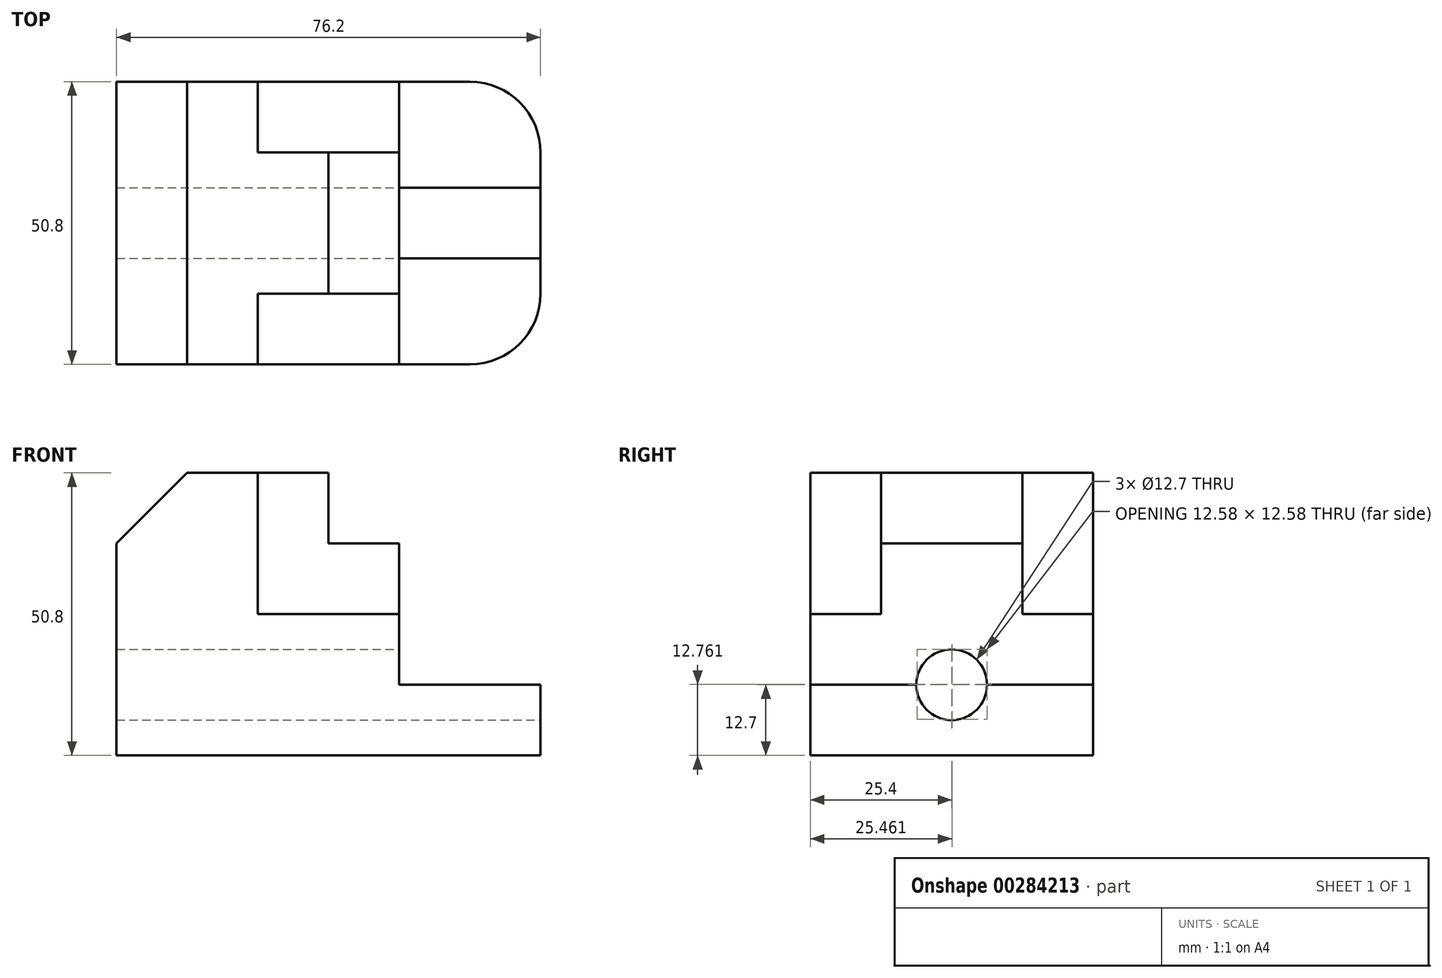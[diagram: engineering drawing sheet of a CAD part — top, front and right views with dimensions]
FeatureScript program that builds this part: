
annotation { "Feature Type Name" : "Feature", "Feature Type Description" : "" }
export const myFeature = defineFeature(function(context is Context, id is Id, definition is map)
    precondition{}
    {
        {
            var Q0;
            Q0=qCreatedBy(makeId("Front.planeOp"),FACE);
            var sketch = newSketch(context, id + "F0", { "sketchPlane" : qUnion([Q0])});
            skLineSegment(sketch, "E0", {"start": v(0, 0) * mm, "end": v(0, 38.1) * mm});
            skLineSegment(sketch, "E1", {"start": v(0, 38.1) * mm, "end": v(12.7, 50.8) * mm});
            skLineSegment(sketch, "E2", {"start": v(12.7, 50.8) * mm, "end": v(38.1, 50.8) * mm});
            skLineSegment(sketch, "E3", {"start": v(38.1, 50.8) * mm, "end": v(38.1, 38.1) * mm});
            skLineSegment(sketch, "E4", {"start": v(38.1, 38.1) * mm, "end": v(50.8, 38.1) * mm});
            skLineSegment(sketch, "E5", {"start": v(50.8, 38.1) * mm, "end": v(50.8, 12.7) * mm});
            skLineSegment(sketch, "E6", {"start": v(50.8, 12.7) * mm, "end": v(76.2, 12.7) * mm});
            skLineSegment(sketch, "E7", {"start": v(76.2, 12.7) * mm, "end": v(76.2, 0) * mm});
            skLineSegment(sketch, "E8", {"start": v(76.2, 0) * mm, "end": v(0, 0) * mm});
            skSolve(sketch);
        }
        {
            var Q0;
            Q0=makeQuery(id+"F0.imprint","IMPRINT",FACE,{"disambiguationData":[TD([[makeQuery(id+"F0.imprint","IMPRINT",EDGE,{"derivedFrom":sQuery(id+"F0.wireOp",EDGE,"E0")}),-1.0]])]});
            extrude(context, id + "F1", {"entities" : qUnion([Q0]), "endBound" : BoundingType.SYMMETRIC, "depth" : 50.8 * mm});
        }
        {
            var Q0;
            Q0=makeQuery(id+"F1.opExtrude","SWEPT_FACE",FACE,{"disambiguationData":[OSD([sQuery(id+"F0.wireOp",EDGE,"E2")])]});
            var sketch = newSketch(context, id + "F2", { "sketchPlane" : qUnion([Q0])});
            skLineSegment(sketch, "E9.bottom", {"start": v(25.4, 25.4) * mm, "end": v(50.8, 25.4) * mm});
            skLineSegment(sketch, "E9.top", {"start": v(25.4, 12.7) * mm, "end": v(50.8, 12.7) * mm});
            skLineSegment(sketch, "E9.left", {"start": v(25.4, 25.4) * mm, "end": v(25.4, 12.7) * mm});
            skLineSegment(sketch, "E9.right", {"start": v(50.8, 25.4) * mm, "end": v(50.8, 12.7) * mm});
            skLineSegment(sketch, "E10.bottom", {"start": v(25.4, -25.4) * mm, "end": v(50.8, -25.4) * mm});
            skLineSegment(sketch, "E10.top", {"start": v(25.4, -12.7) * mm, "end": v(50.8, -12.7) * mm});
            skLineSegment(sketch, "E10.left", {"start": v(25.4, -25.4) * mm, "end": v(25.4, -12.7) * mm});
            skLineSegment(sketch, "E10.right", {"start": v(50.8, -25.4) * mm, "end": v(50.8, -12.7) * mm});
            skSolve(sketch);
        }
        {
            var Q0;
            {var subQ4=sQuery(id+"F2.wireOp",EDGE,"E9.left");Q0=makeQuery(id+"F2.imprint","IMPRINT",FACE,{"disambiguationData":[TD([[makeQuery(id+"F2.imprint","IMPRINT",EDGE,{"derivedFrom":subQ4}),1.0]])]});}
            extrude(context, id + "F3", {"entities" : qUnion([Q0]), "operationType" : NewBodyOperationType.REMOVE, "oppositeDirection" : true, "depth" : 25.4 * mm});
        }
        {
            var Q0;
            {var subQ4=sQuery(id+"F2.wireOp",EDGE,"E10.left");Q0=makeQuery(id+"F2.imprint","IMPRINT",FACE,{"disambiguationData":[TD([[makeQuery(id+"F2.imprint","IMPRINT",EDGE,{"derivedFrom":subQ4}),-1.0]])]});}
            extrude(context, id + "F4", {"entities" : qUnion([Q0]), "operationType" : NewBodyOperationType.REMOVE, "oppositeDirection" : true, "depth" : 25.4 * mm});
        }
        {
            var Q0;
            Q0=makeQuery(id+"F1.opExtrude","CAP_FACE",FACE,{"disambiguationData":[OSD([sQuery(id+"F0.wireOp",EDGE,"E0"),sQuery(id+"F0.wireOp",EDGE,"E1"),sQuery(id+"F0.wireOp",EDGE,"E2"),sQuery(id+"F0.wireOp",EDGE,"E3"),sQuery(id+"F0.wireOp",EDGE,"E4"),sQuery(id+"F0.wireOp",EDGE,"E5"),sQuery(id+"F0.wireOp",EDGE,"E6"),sQuery(id+"F0.wireOp",EDGE,"E7"),sQuery(id+"F0.wireOp",EDGE,"E8")])],"isStart":false});
            var sketch = newSketch(context, id + "F5", { "sketchPlane" : qUnion([Q0])});
            skLineSegment(sketch, "E11.bottom", {"start": v(38.1, 38.1) * mm, "end": v(50.8, 38.1) * mm});
            skLineSegment(sketch, "E11.top", {"start": v(38.1, 25.4) * mm, "end": v(50.8, 25.4) * mm});
            skLineSegment(sketch, "E11.left", {"start": v(38.1, 38.1) * mm, "end": v(38.1, 25.4) * mm});
            skLineSegment(sketch, "E11.right", {"start": v(50.8, 38.1) * mm, "end": v(50.8, 25.4) * mm});
            skSolve(sketch);
        }
        {
            var Q0;
            Q0=makeQuery(id+"F5.imprint","IMPRINT",FACE,{"disambiguationData":[TD([[makeQuery(id+"F5.imprint","IMPRINT",EDGE,{"derivedFrom":sQuery(id+"F5.wireOp",EDGE,"E11.bottom")}),-1.0]])]});
            extrude(context, id + "F6", {"entities" : qUnion([Q0]), "operationType" : NewBodyOperationType.REMOVE, "oppositeDirection" : true, "depth" : 12.7 * mm});
        }
        {
            var Q0;
            Q0=makeQuery(id+"F1.opExtrude","CAP_FACE",FACE,{"disambiguationData":[OSD([sQuery(id+"F0.wireOp",EDGE,"E0"),sQuery(id+"F0.wireOp",EDGE,"E1"),sQuery(id+"F0.wireOp",EDGE,"E2"),sQuery(id+"F0.wireOp",EDGE,"E3"),sQuery(id+"F0.wireOp",EDGE,"E4"),sQuery(id+"F0.wireOp",EDGE,"E5"),sQuery(id+"F0.wireOp",EDGE,"E6"),sQuery(id+"F0.wireOp",EDGE,"E7"),sQuery(id+"F0.wireOp",EDGE,"E8")])],"isStart":true});
            var sketch = newSketch(context, id + "F7", { "sketchPlane" : qUnion([Q0])});
            skLineSegment(sketch, "E12.bottom", {"start": v(-50.8, 38.1) * mm, "end": v(-38.1, 38.1) * mm});
            skLineSegment(sketch, "E12.top", {"start": v(-50.8, 25.4) * mm, "end": v(-38.1, 25.4) * mm});
            skLineSegment(sketch, "E12.left", {"start": v(-50.8, 38.1) * mm, "end": v(-50.8, 25.4) * mm});
            skLineSegment(sketch, "E12.right", {"start": v(-38.1, 38.1) * mm, "end": v(-38.1, 25.4) * mm});
            skSolve(sketch);
        }
        {
            var Q0;
            Q0=makeQuery(id+"F7.imprint","IMPRINT",FACE,{"disambiguationData":[TD([[makeQuery(id+"F7.imprint","IMPRINT",EDGE,{"derivedFrom":sQuery(id+"F7.wireOp",EDGE,"E12.bottom")}),1.0]])]});
            extrude(context, id + "F8", {"entities" : qUnion([Q0]), "operationType" : NewBodyOperationType.REMOVE, "oppositeDirection" : true, "depth" : 12.7 * mm});
        }
        {
            var Q0;
            Q0=makeQuery(id+"F1.opExtrude","SWEPT_FACE",FACE,{"disambiguationData":[OSD([sQuery(id+"F0.wireOp",EDGE,"E7")])]});
            var sketch = newSketch(context, id + "F9", { "sketchPlane" : qUnion([Q0])});
            skCircle(sketch, "E13", {"center": v(0, 12.7) * mm, "radius": 6.35 * mm});
            skSolve(sketch);
        }
        {
            var Q0;
            {var subQ0=sQuery(id+"F9.wireOp",EDGE,"E13");var subQ1=makeQuery(id+"F1.opExtrude","SWEPT_EDGE",EDGE,{"disambiguationData":[OSD([sQuery(id+"F0.wireOp",EDGE,"E6"),sQuery(id+"F0.wireOp",EDGE,"E7")])]});var subQ2=makeQuery(id+"F9.imprint","INTERSECT",VERTEX,{"disambiguationData":[OD(0.0)],"derivedFrom":[subQ1,subQ0]});Q0=makeQuery(id+"F9.imprint","IMPRINT",FACE,{"disambiguationData":[TD([[makeQuery(id+"F9.imprint","IMPRINT",EDGE,{"disambiguationData":[TD([[subQ2,1.0]])],"derivedFrom":subQ0}),1.0]])]});}
            var Q1;
            {var subQ0=sQuery(id+"F9.wireOp",EDGE,"E13");var subQ1=makeQuery(id+"F1.opExtrude","SWEPT_EDGE",EDGE,{"disambiguationData":[OSD([sQuery(id+"F0.wireOp",EDGE,"E6"),sQuery(id+"F0.wireOp",EDGE,"E7")])]});var subQ2=makeQuery(id+"F9.imprint","INTERSECT",VERTEX,{"disambiguationData":[OD(0.0)],"derivedFrom":[subQ1,subQ0]});Q1=makeQuery(id+"F9.imprint","IMPRINT",FACE,{"disambiguationData":[TD([[makeQuery(id+"F9.imprint","IMPRINT",EDGE,{"disambiguationData":[TD([[subQ2,-1.0]])],"derivedFrom":subQ0}),1.0]])]});}
            extrude(context, id + "F10", {"entities" : qUnion([Q0, Q1]), "operationType" : NewBodyOperationType.REMOVE, "endBound" : BoundingType.THROUGH_ALL, "oppositeDirection" : true, "depth" : 25.4 * mm});
        }
        {
            var Q0;
            Q0=makeQuery(id+"F1.opExtrude","CAP_EDGE",EDGE,{"disambiguationData":[OSD([sQuery(id+"F0.wireOp",EDGE,"E7")])],"isStart":false});
            var Q1;
            Q1=makeQuery(id+"F1.opExtrude","CAP_EDGE",EDGE,{"disambiguationData":[OSD([sQuery(id+"F0.wireOp",EDGE,"E7")])],"isStart":true});
            fillet(context, id + "F11", {"entities" : qUnion([Q0, Q1]), "radius" : 12.7 * mm, "tangentPropagation" : true, "allowEdgeOverflow" : false});
        }
    });
